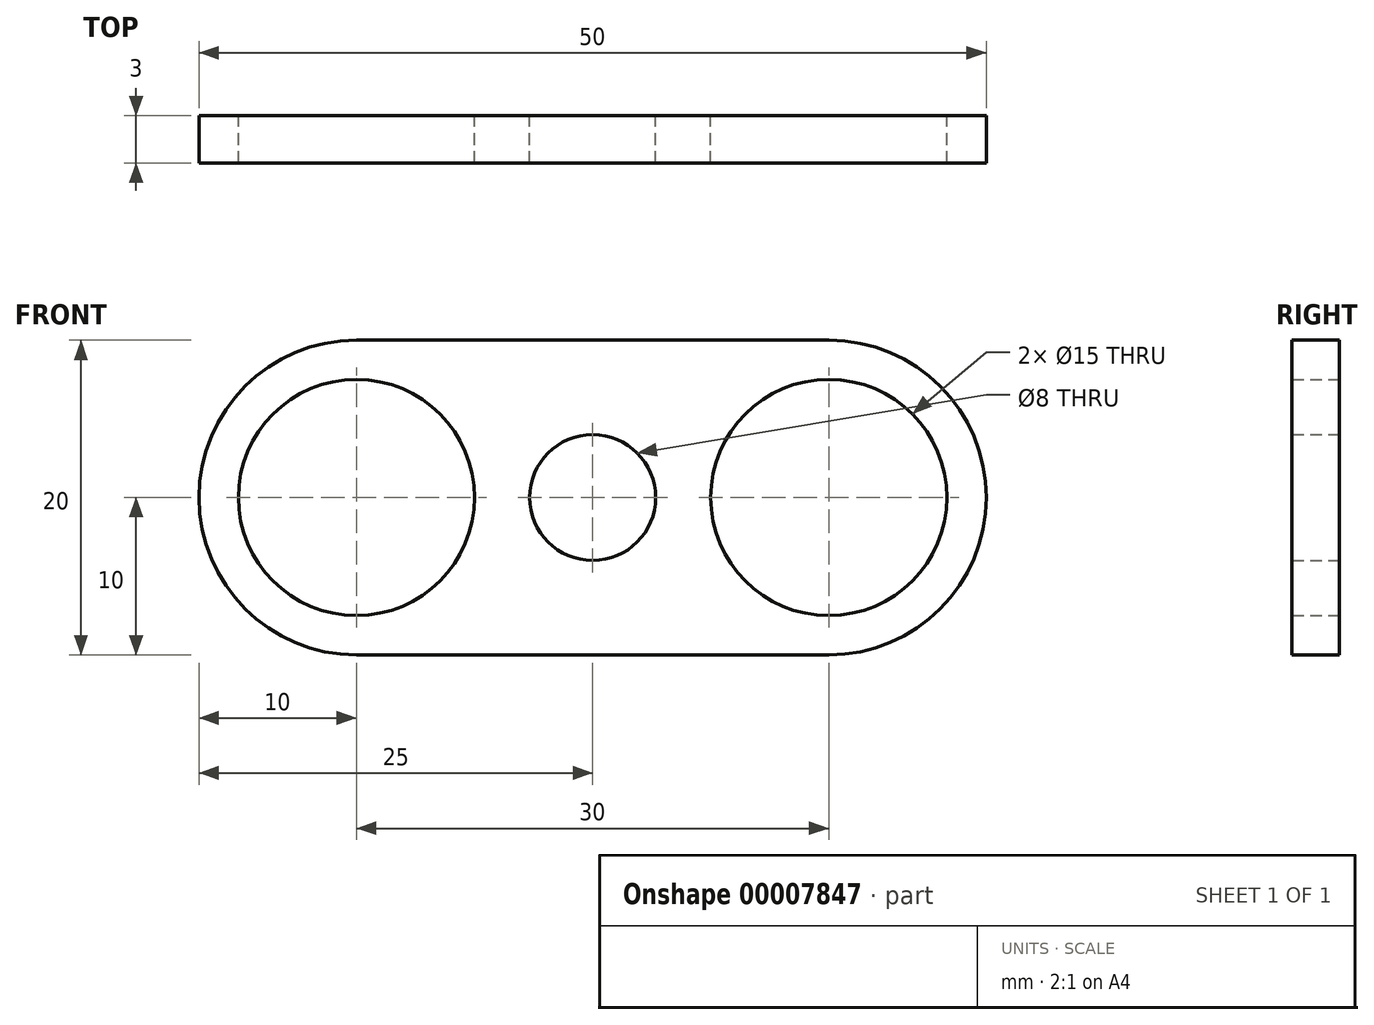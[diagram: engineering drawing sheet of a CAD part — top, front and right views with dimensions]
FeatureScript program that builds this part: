
annotation { "Feature Type Name" : "Feature", "Feature Type Description" : "" }
export const myFeature = defineFeature(function(context is Context, id is Id, definition is map)
    precondition{}
    {
        {
            var Q0;
            Q0=qCreatedBy(makeId("Front.planeOp"),FACE);
            var sketch = newSketch(context, id + "F0", { "sketchPlane" : qUnion([Q0])});
            skCircle(sketch, "E0", {"center": v(-15, 0) * mm, "radius": 7.5 * mm});
            skCircle(sketch, "E1", {"center": v(15, 0) * mm, "radius": 7.5 * mm});
            skArc(sketch, "E2", {"start": v(-15, 10) * mm, "mid": v(-25, 0) * mm, "end": v(-15, -10) * mm});
            skArc(sketch, "E3", {"start": v(15, -10) * mm, "mid": v(25, 0) * mm, "end": v(15, 10) * mm});
            skLineSegment(sketch, "E4", {"start": v(-15, 10) * mm, "end": v(15, 10) * mm});
            skLineSegment(sketch, "E5", {"start": v(-15, -10) * mm, "end": v(15, -10) * mm});
            skCircle(sketch, "E6", {"center": v(0, 0) * mm, "radius": 4 * mm});
            skSolve(sketch);
        }
        {
            var Q0;
            Q0=makeQuery(id+"F0.imprint","IMPRINT",FACE,{"disambiguationData":[TD([[makeQuery(id+"F0.imprint","IMPRINT",EDGE,{"derivedFrom":sQuery(id+"F0.wireOp",EDGE,"E0")}),-1.0]])]});
            extrude(context, id + "F1", {"entities" : qUnion([Q0]), "depth" : 3 * mm});
        }
    });
